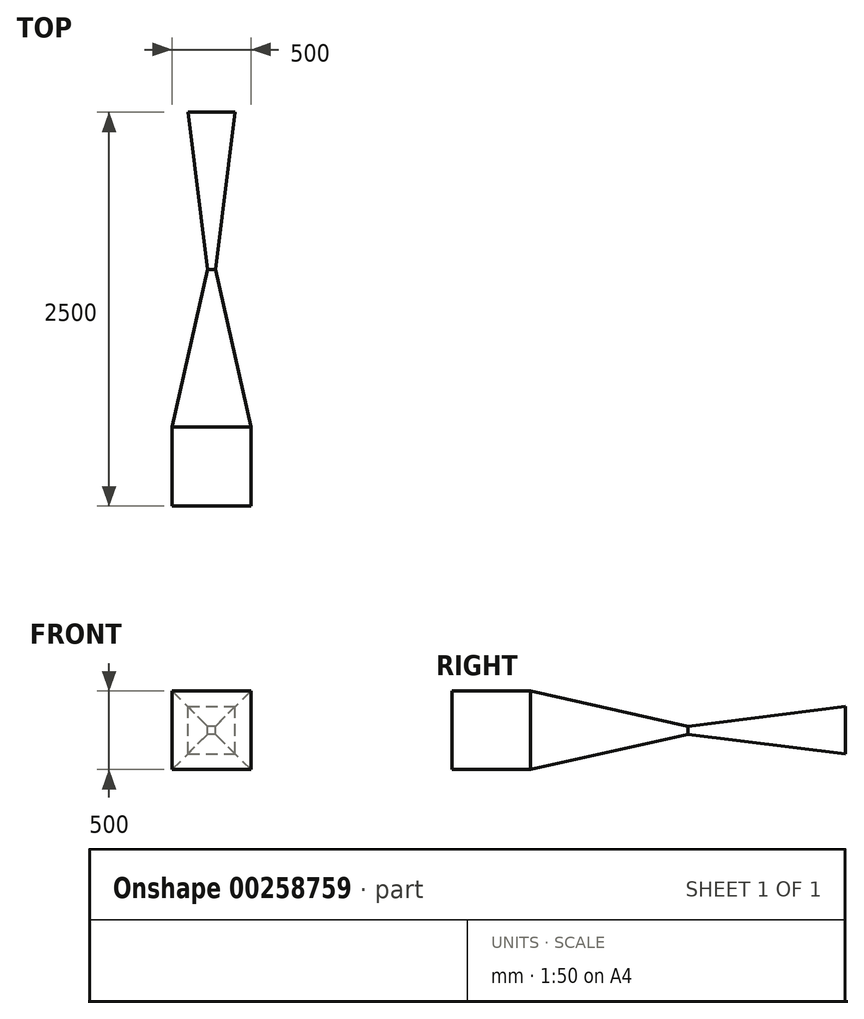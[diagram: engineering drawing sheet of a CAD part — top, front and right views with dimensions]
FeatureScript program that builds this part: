
annotation { "Feature Type Name" : "Feature", "Feature Type Description" : "" }
export const myFeature = defineFeature(function(context is Context, id is Id, definition is map)
    precondition{}
    {
        {
            var Q0;
            Q0=qCreatedBy(makeId("Front.planeOp"),FACE);
            cPlane(context, id + "F0", {"entities" : qUnion([Q0]), "cplaneType" : CPlaneType.OFFSET, "offset" : 1000 * mm, "width" : 150 * mm, "height" : 150 * mm});
        }
        {
            var Q0;
            Q0=qCreatedBy(makeId("Front.planeOp"),FACE);
            var sketch = newSketch(context, id + "F1", { "sketchPlane" : qUnion([Q0])});
            skLineSegment(sketch, "E0.bottom", {"start": v(25, -25) * mm, "end": v(-25, -25) * mm});
            skLineSegment(sketch, "E0.top", {"start": v(25, 25) * mm, "end": v(-25, 25) * mm});
            skLineSegment(sketch, "E0.left", {"start": v(25, -25) * mm, "end": v(25, 25) * mm});
            skLineSegment(sketch, "E0.right", {"start": v(-25, -25) * mm, "end": v(-25, 25) * mm});
            skPoint(sketch, "E0.middle", {"position": v(0, 0) * mm});
            skSolve(sketch);
        }
        {
            var Q0;
            Q0=qCreatedBy(id+"F0.planeOp",FACE);
            var sketch = newSketch(context, id + "F2", { "sketchPlane" : qUnion([Q0])});
            skLineSegment(sketch, "E1.bottom", {"start": v(250, -250) * mm, "end": v(-250, -250) * mm});
            skLineSegment(sketch, "E1.top", {"start": v(250, 250) * mm, "end": v(-250, 250) * mm});
            skLineSegment(sketch, "E1.left", {"start": v(250, -250) * mm, "end": v(250, 250) * mm});
            skLineSegment(sketch, "E1.right", {"start": v(-250, -250) * mm, "end": v(-250, 250) * mm});
            skPoint(sketch, "E1.middle", {"position": v(0, 0) * mm});
            skSolve(sketch);
        }
        {
            var Q0;
            Q0=makeQuery(id+"F2.imprint","IMPRINT",FACE,{"disambiguationData":[TD([[makeQuery(id+"F2.imprint","IMPRINT",EDGE,{"derivedFrom":sQuery(id+"F2.wireOp",EDGE,"E1.bottom")}),-1.0]])]});
            var Q1;
            Q1=makeQuery(id+"F1.imprint","IMPRINT",FACE,{"disambiguationData":[TD([[makeQuery(id+"F1.imprint","IMPRINT",EDGE,{"derivedFrom":sQuery(id+"F1.wireOp",EDGE,"E0.bottom")}),-1.0]])]});
            loft(context, id + "F3", {"sheetProfilesArray" : [{ "sheetProfileEntities" : qUnion([Q0]) }, { "sheetProfileEntities" : qUnion([Q1]) }]});
        }
        {
            var Q0;
            Q0=qCreatedBy(makeId("Front.planeOp"),FACE);
            cPlane(context, id + "F4", {"entities" : qUnion([Q0]), "cplaneType" : CPlaneType.OFFSET, "offset" : 1000 * mm, "oppositeDirection" : true, "width" : 150 * mm, "height" : 150 * mm});
        }
        {
            var Q0;
            Q0=qCreatedBy(id+"F4.planeOp",FACE);
            var sketch = newSketch(context, id + "F5", { "sketchPlane" : qUnion([Q0])});
            skLineSegment(sketch, "E2.bottom", {"start": v(-150, -150) * mm, "end": v(150, -150) * mm});
            skLineSegment(sketch, "E2.top", {"start": v(-150, 150) * mm, "end": v(150, 150) * mm});
            skLineSegment(sketch, "E2.left", {"start": v(-150, -150) * mm, "end": v(-150, 150) * mm});
            skLineSegment(sketch, "E2.right", {"start": v(150, -150) * mm, "end": v(150, 150) * mm});
            skPoint(sketch, "E2.middle", {"position": v(0, 0) * mm});
            skSolve(sketch);
        }
        {
            var Q1;
            Q1 = qSketchRegion(id + "F1", true);
            var Q2;
            Q2 = qSketchRegion(id + "F5", true);
            loft(context, id + "F6", {"operationType" : NewBodyOperationType.ADD, "sheetProfilesArray" : [{ "sheetProfileEntities" : qUnion([Q1]) }, { "sheetProfileEntities" : qUnion([Q2]) }]});
        }
        {
            var Q0;
            Q0=makeQuery(id+"F3.opLoft","CAP_FACE",FACE,{"disambiguationData":[OSD([makeQuery(id+"F2.imprint","IMPRINT",FACE,{"disambiguationData":[TD([[makeQuery(id+"F2.imprint","IMPRINT",EDGE,{"derivedFrom":sQuery(id+"F2.wireOp",EDGE,"E1.bottom")}),-1.0]])]})])],"isStart":true});
            extrude(context, id + "F7", {"entities" : qUnion([Q0]), "operationType" : NewBodyOperationType.ADD, "depth" : 500 * mm});
        }
    });
